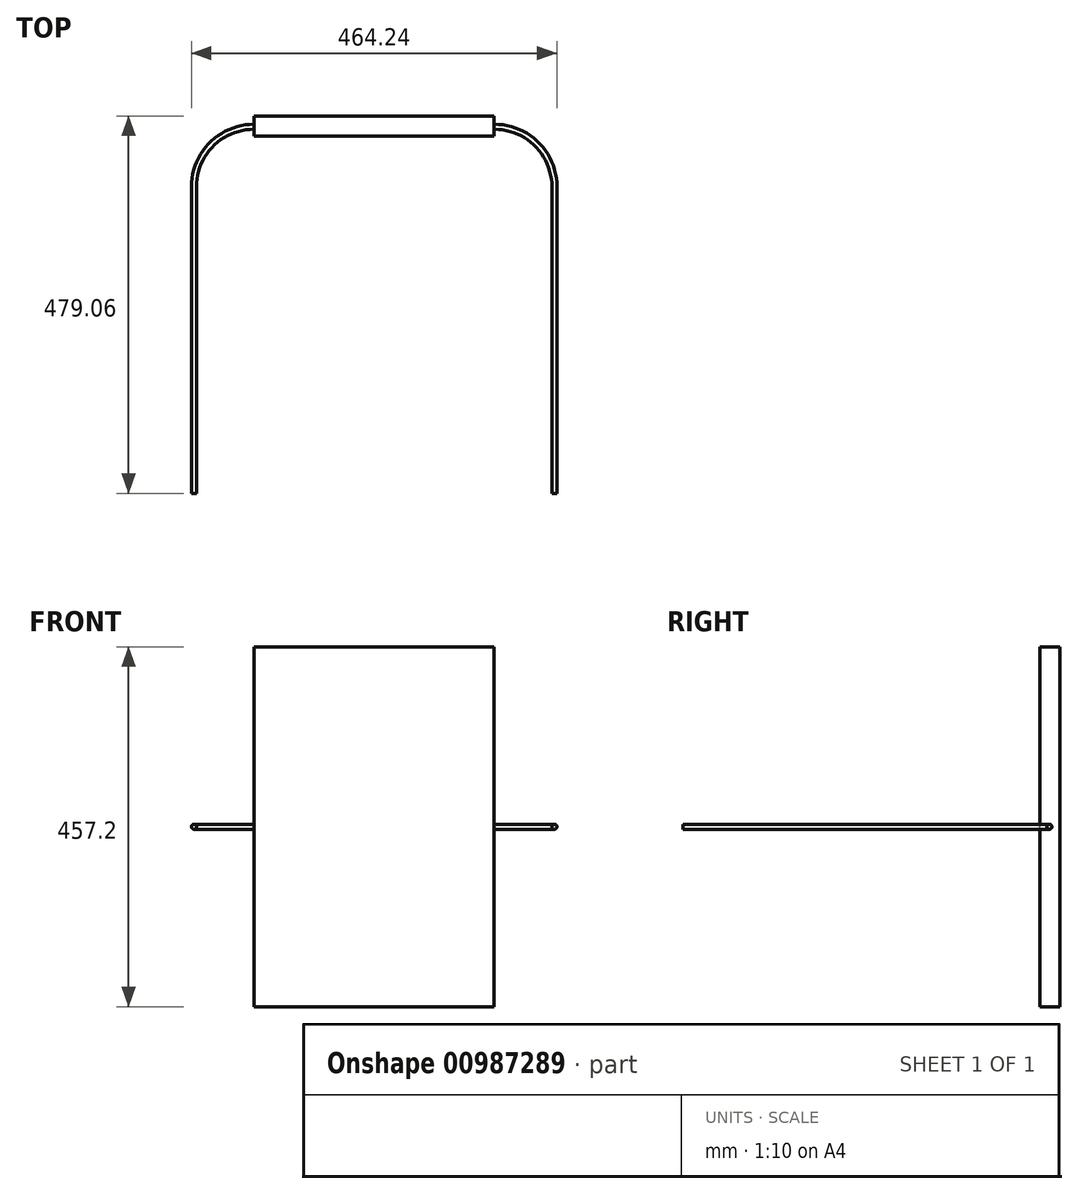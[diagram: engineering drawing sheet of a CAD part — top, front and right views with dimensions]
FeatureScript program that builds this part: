
annotation { "Feature Type Name" : "Feature", "Feature Type Description" : "" }
export const myFeature = defineFeature(function(context is Context, id is Id, definition is map)
    precondition{}
    {
        {
            var Q0;
            Q0=qCreatedBy(makeId("Top.planeOp"),FACE);
            var sketch = newSketch(context, id + "F0", { "sketchPlane" : qUnion([Q0])});
            skLineSegment(sketch, "E0.top", {"start": v(152.74, 232.8) * mm, "end": v(-152.74, 232.8) * mm});
            skLineSegment(sketch, "E0.left", {"start": v(228.94, -232.8) * mm, "end": v(228.94, 156.6) * mm});
            skLineSegment(sketch, "E0.right", {"start": v(-228.94, -232.8) * mm, "end": v(-228.94, 156.6) * mm});
            skPoint(sketch, "E0.middle", {"position": v(0, 0) * mm});
            skPoint(sketch, "E1.visualSharp", {"position": v(-228.94, 232.8) * mm});
            skArc(sketch, "E1.filletArc", {"start": v(-152.74, 232.8) * mm, "mid": v(-206.62, 210.48) * mm, "end": v(-228.94, 156.6) * mm});
            skPoint(sketch, "E2.visualSharp", {"position": v(228.94, 232.8) * mm});
            skArc(sketch, "E2.filletArc", {"start": v(228.94, 156.6) * mm, "mid": v(206.62, 210.48) * mm, "end": v(152.74, 232.8) * mm});
            skPoint(sketch, "E3.visualSharp", {"position": v(-228.94, -232.8) * mm});
            skPoint(sketch, "E4.visualSharp", {"position": v(228.94, -232.8) * mm});
            skSolve(sketch);
        }
        {
            var Q0;
            Q0=qCreatedBy(makeId("Front.planeOp"),FACE);
            var sketch = newSketch(context, id + "F1", { "sketchPlane" : qUnion([Q0])});
            skCircle(sketch, "E5", {"center": v(-228.94, 0) * mm, "radius": 3.18 * mm});
            skSolve(sketch);
        }
        {
            var Q0;
            Q0 = qSketchRegion(id + "F1", true);
            var Q1;
            Q1 = qConstructionFilter(qBodyType(qCreatedBy(id + "F0" ,EDGE), BodyType.WIRE), ConstructionObject.NO);
            sweep(context, id + "F2", {"profiles" : qUnion([Q0]), "path" : qUnion([Q1])});
        }
        {
            var Q0;
            Q0=qCreatedBy(makeId("Top.planeOp"),FACE);
            var sketch = newSketch(context, id + "F3", { "sketchPlane" : qUnion([Q0])});
            skLineSegment(sketch, "E6.bottom", {"start": v(-152.4, 246.26) * mm, "end": v(152.4, 246.26) * mm});
            skLineSegment(sketch, "E6.top", {"start": v(-152.4, 220.86) * mm, "end": v(152.4, 220.86) * mm});
            skLineSegment(sketch, "E6.left", {"start": v(-152.4, 246.26) * mm, "end": v(-152.4, 220.86) * mm});
            skLineSegment(sketch, "E6.right", {"start": v(152.4, 246.26) * mm, "end": v(152.4, 220.86) * mm});
            skPoint(sketch, "E6.middle", {"position": v(0, 233.56) * mm});
            skSolve(sketch);
        }
        {
            var Q0;
            Q0 = qSketchRegion(id + "F3", true);
            extrude(context, id + "F4", {"entities" : qUnion([Q0]), "operationType" : NewBodyOperationType.ADD, "endBound" : BoundingType.SYMMETRIC, "oppositeDirection" : true, "depth" : 457.2 * mm, "offsetDistance" : 25.4 * mm});
        }
    });
